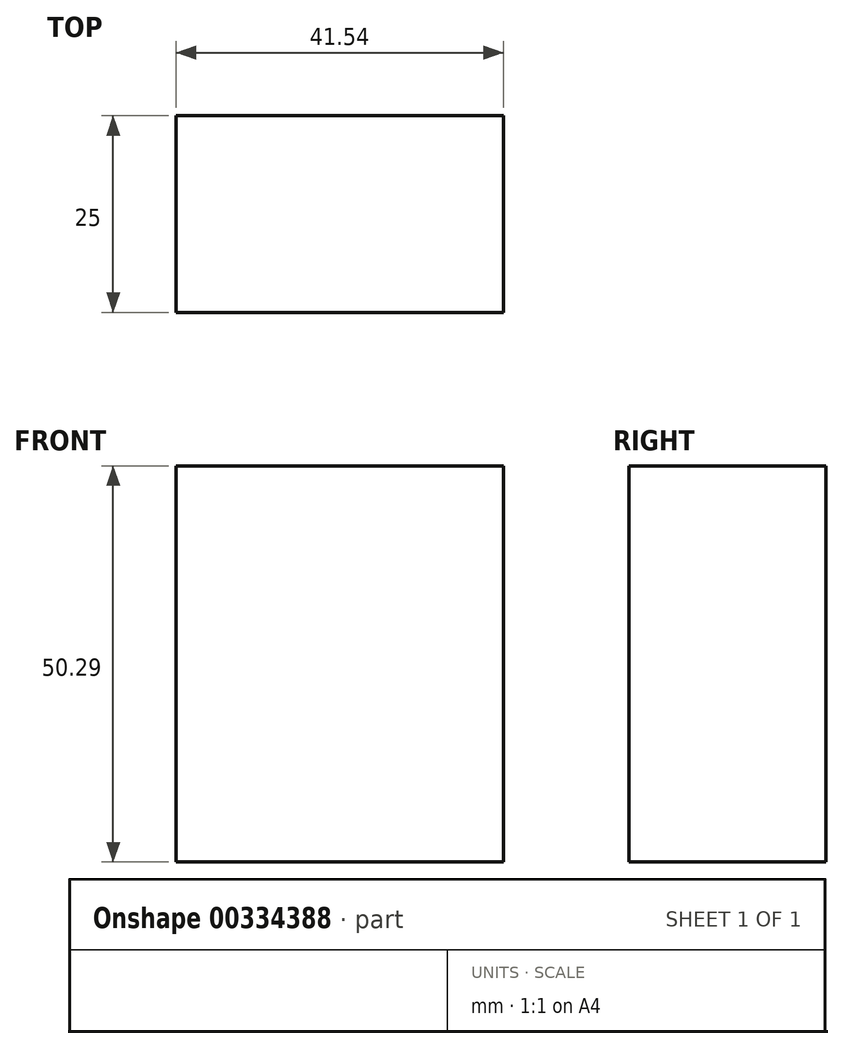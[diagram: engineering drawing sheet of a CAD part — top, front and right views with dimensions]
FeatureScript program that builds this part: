
annotation { "Feature Type Name" : "Feature", "Feature Type Description" : "" }
export const myFeature = defineFeature(function(context is Context, id is Id, definition is map)
    precondition{}
    {
        {
            var Q0;
            Q0=qCreatedBy(makeId("Front.planeOp"),FACE);
            var sketch = newSketch(context, id + "F0", { "sketchPlane" : qUnion([Q0])});
            skLineSegment(sketch, "E0.bottom", {"start": v(-157.41, -6.17) * mm, "end": v(-115.87, -6.17) * mm});
            skLineSegment(sketch, "E0.top", {"start": v(-157.41, 44.12) * mm, "end": v(-115.87, 44.12) * mm});
            skLineSegment(sketch, "E0.left", {"start": v(-157.41, -6.17) * mm, "end": v(-157.41, 44.12) * mm});
            skLineSegment(sketch, "E0.right", {"start": v(-115.87, -6.17) * mm, "end": v(-115.87, 44.12) * mm});
            skPoint(sketch, "E0.middle", {"position": v(-136.64, 18.98) * mm});
            skSolve(sketch);
        }
        {
            var Q0;
            Q0=makeQuery(id+"F0.imprint","IMPRINT",FACE,{"disambiguationData":[TD([[makeQuery(id+"F0.imprint","IMPRINT",EDGE,{"derivedFrom":sQuery(id+"F0.wireOp",EDGE,"E0.bottom")}),1.0]])]});
            extrude(context, id + "F1", {"entities" : qUnion([Q0]), "depth" : 25 * mm});
        }
    });
